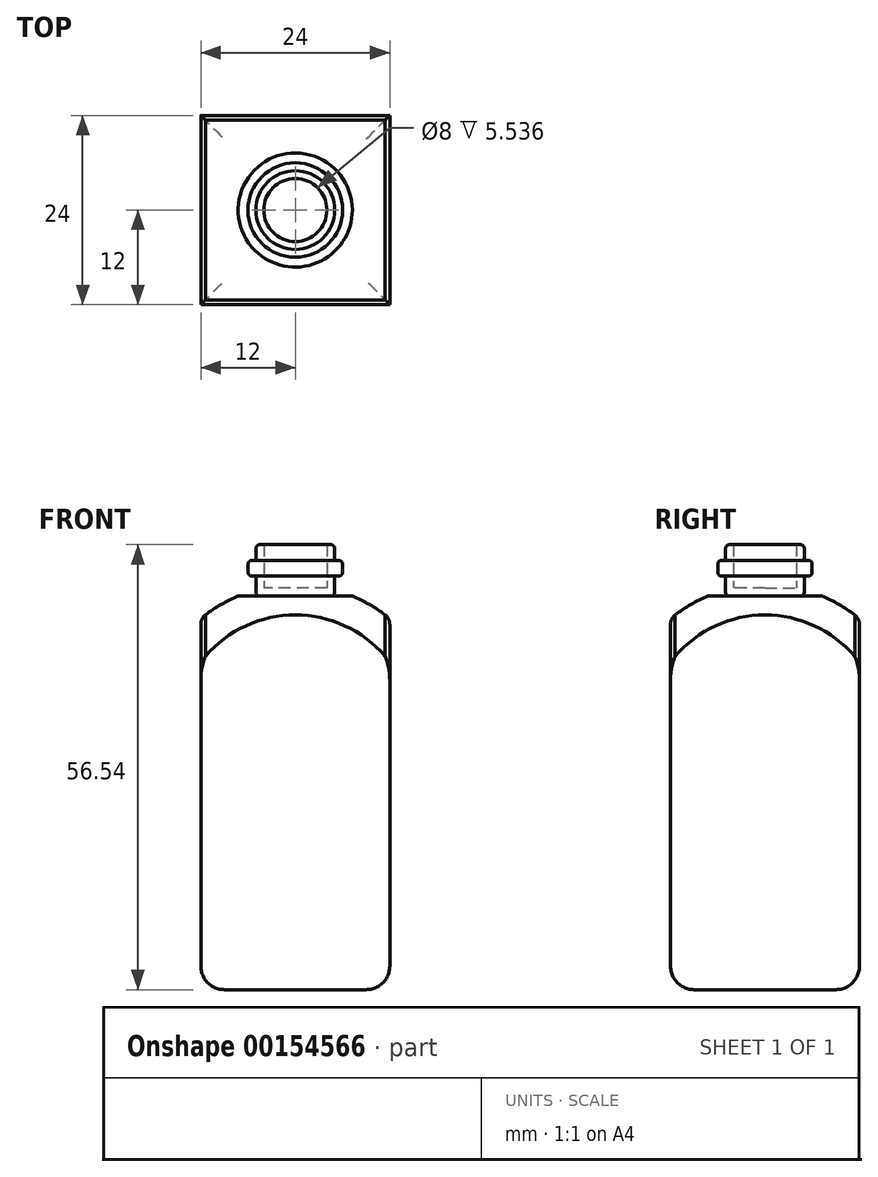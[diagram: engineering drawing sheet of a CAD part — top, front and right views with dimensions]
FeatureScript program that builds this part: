
annotation { "Feature Type Name" : "Feature", "Feature Type Description" : "" }
export const myFeature = defineFeature(function(context is Context, id is Id, definition is map)
    precondition{}
    {
        {
            var Q0;
            Q0=qCreatedBy(makeId("Front.planeOp"),FACE);
            var sketch = newSketch(context, id + "F0", { "sketchPlane" : qUnion([Q0])});
            skLineSegment(sketch, "E0", {"start": v(0, 56.54) * mm, "end": v(-5, 56.54) * mm});
            skLineSegment(sketch, "E1", {"start": v(-5, 56.54) * mm, "end": v(-5, 54.54) * mm});
            skLineSegment(sketch, "E2", {"start": v(-5, 54.54) * mm, "end": v(-6, 54.54) * mm});
            skLineSegment(sketch, "E3", {"start": v(-6, 54.54) * mm, "end": v(-6, 52.54) * mm});
            skLineSegment(sketch, "E4", {"start": v(-6, 52.54) * mm, "end": v(-5, 52.54) * mm});
            skLineSegment(sketch, "E5", {"start": v(-5, 52.54) * mm, "end": v(-5, 50) * mm});
            skLineSegment(sketch, "E6", {"start": v(-5, 50) * mm, "end": v(-12, 50) * mm});
            skLineSegment(sketch, "E7", {"start": v(-12, 50) * mm, "end": v(-12, 0) * mm});
            skLineSegment(sketch, "E8", {"start": v(-12, 0) * mm, "end": v(0, 0) * mm});
            skLineSegment(sketch, "E9", {"start": v(0, 0) * mm, "end": v(0, 56.54) * mm});
            skLineSegment(sketch, "E10.MirrorCS", {"start": v(5, 50) * mm, "end": v(12, 50) * mm});
            skLineSegment(sketch, "E11.MirrorCS", {"start": v(12, 50) * mm, "end": v(12, 0) * mm});
            skLineSegment(sketch, "E12.MirrorCS", {"start": v(12, 0) * mm, "end": v(0, 0) * mm});
            skLineSegment(sketch, "E13.MirrorCS", {"start": v(0, 56.54) * mm, "end": v(5, 56.54) * mm});
            skLineSegment(sketch, "E14.MirrorCS", {"start": v(5, 56.54) * mm, "end": v(5, 54.54) * mm});
            skLineSegment(sketch, "E15.MirrorCS", {"start": v(5, 54.54) * mm, "end": v(6, 54.54) * mm});
            skLineSegment(sketch, "E16.MirrorCS", {"start": v(6, 54.54) * mm, "end": v(6, 52.54) * mm});
            skLineSegment(sketch, "E17.MirrorCS", {"start": v(6, 52.54) * mm, "end": v(5, 52.54) * mm});
            skLineSegment(sketch, "E18.MirrorCS", {"start": v(5, 52.54) * mm, "end": v(5, 50) * mm});
            skLineSegment(sketch, "E19", {"start": v(-5, 50) * mm, "end": v(5, 50) * mm});
            skArc(sketch, "E20", {"start": v(-5, 50) * mm, "mid": v(-9.2, 47.2) * mm, "end": v(-12, 43) * mm});
            skPoint(sketch, "E21", {"position": v(0, 50) * mm});
            skSolve(sketch);
        }
        {
            var Q0;
            Q0=makeQuery(id+"F0.imprint","IMPRINT",FACE,{"disambiguationData":[TD([[makeQuery(id+"F0.imprint","IMPRINT",EDGE,{"derivedFrom":sQuery(id+"F0.wireOp",EDGE,"E9")}),-1.0]])]});
            var Q1;
            {var subQ4=sQuery(id+"F0.wireOp",EDGE,"E6");Q1=makeQuery(id+"F0.imprint","IMPRINT",FACE,{"disambiguationData":[TD([[makeQuery(id+"F0.imprint","IMPRINT",EDGE,{"derivedFrom":subQ4}),1.0]])]});}
            var Q2;
            {var subQ1=sQuery(id+"F0.wireOp",EDGE,"E8");Q2=makeQuery(id+"F0.imprint","IMPRINT",FACE,{"disambiguationData":[TD([[makeQuery(id+"F0.imprint","IMPRINT",EDGE,{"derivedFrom":subQ1}),1.0]])]});}
            extrude(context, id + "F1", {"entities" : qUnion([Q0, Q1, Q2]), "depth" : 12 * mm, "hasSecondDirection" : true, "secondDirectionOppositeDirection" : true, "secondDirectionDepth" : 12 * mm});
        }
        {
            var Q0;
            {var subQ1=sQuery(id+"F0.wireOp",EDGE,"E0");Q0=makeQuery(id+"F0.imprint","IMPRINT",FACE,{"disambiguationData":[TD([[makeQuery(id+"F0.imprint","IMPRINT",EDGE,{"derivedFrom":subQ1}),1.0]])]});}
            var Q1;
            Q1=sQuery(id+"F0.wireOp",EDGE,"E9");
            revolve(context, id + "F2", {"entities" : qUnion([Q0]), "axis" : qUnion([Q1]), "revolveType" : RevolveType.FULL});
        }
        {
            var Q0;
            Q0=makeQuery(id+"F2.opRevolve","SWEPT_EDGE",EDGE,{"disambiguationData":[OSD([sQuery(id+"F0.wireOp",EDGE,"E0"),sQuery(id+"F0.wireOp",EDGE,"E1")])]});
            var Q1;
            Q1=makeQuery(id+"F2.opRevolve","SWEPT_EDGE",EDGE,{"disambiguationData":[OSD([sQuery(id+"F0.wireOp",EDGE,"E2"),sQuery(id+"F0.wireOp",EDGE,"E3")])]});
            var Q2;
            Q2=makeQuery(id+"F2.opRevolve","SWEPT_EDGE",EDGE,{"disambiguationData":[OSD([sQuery(id+"F0.wireOp",EDGE,"E3"),sQuery(id+"F0.wireOp",EDGE,"E4")])]});
            var Q3;
            Q3=makeQuery(id+"F2.opRevolve","SWEPT_EDGE",EDGE,{"disambiguationData":[OSD([sQuery(id+"F0.wireOp",EDGE,"E5"),sQuery(id+"F0.wireOp",EDGE,"E6"),sQuery(id+"F0.wireOp",EDGE,"E19")])]});
            var Q4;
            Q4=makeQuery(id+"FP4xKetyCxuXSmg_1.boolean.opBoolean","COPY",EDGE,{"derivedFrom":makeQuery(id+"FP4xKetyCxuXSmg_1.boolean.toolComplement.opBoolean","COPY",EDGE,{"derivedFrom":makeQuery(id+"FP4xKetyCxuXSmg_1.opRevolve","SWEPT_EDGE",EDGE,{"disambiguationData":[OSD([sQuery(id+"F0.wireOp",EDGE,"E6"),sQuery(id+"F0.wireOp",EDGE,"SgCcnmhd-jZyr-n1Pt-VPxV-8aRdMBWvmJDz")])]})})});
            var Q5;
            Q5=makeQuery(id+"FP4xKetyCxuXSmg_1.boolean.opBoolean","COPY",EDGE,{"disambiguationData":[OD(0.0)],"derivedFrom":makeQuery(id+"FP4xKetyCxuXSmg_1.boolean.toolComplement.opBoolean","COPY",EDGE,{"derivedFrom":makeQuery(id+"FP4xKetyCxuXSmg_1.opRevolve","SWEPT_EDGE",EDGE,{"disambiguationData":[OSD([sQuery(id+"F0.wireOp",EDGE,"E7"),sQuery(id+"F0.wireOp",EDGE,"SgCcnmhd-jZyr-n1Pt-VPxV-8aRdMBWvmJDz")])]})})});
            var Q6;
            Q6=makeQuery(id+"FP4xKetyCxuXSmg_1.boolean.opBoolean","COPY",EDGE,{"disambiguationData":[OD(1.0)],"derivedFrom":makeQuery(id+"FP4xKetyCxuXSmg_1.boolean.toolComplement.opBoolean","COPY",EDGE,{"derivedFrom":makeQuery(id+"FP4xKetyCxuXSmg_1.opRevolve","SWEPT_EDGE",EDGE,{"disambiguationData":[OSD([sQuery(id+"F0.wireOp",EDGE,"E7"),sQuery(id+"F0.wireOp",EDGE,"SgCcnmhd-jZyr-n1Pt-VPxV-8aRdMBWvmJDz")])]})})});
            fillet(context, id + "F3", {"entities" : qUnion([Q0, Q1, Q2, Q3, Q4, Q5, Q6]), "radius" : .5 * mm, "allowEdgeOverflow" : false});
        }
        {
            var Q0;
            {var subQ0=sQuery(id+"F0.wireOp",EDGE,"E6");Q0=makeQuery(id+"F0.imprint","IMPRINT",FACE,{"disambiguationData":[TD([[makeQuery(id+"F0.imprint","IMPRINT",EDGE,{"derivedFrom":subQ0}),1.0]])]});}
            var Q1;
            Q1=sQuery(id+"F0.wireOp",EDGE,"E20");
            var Q2;
            Q2=sQuery(id+"F0.wireOp",EDGE,"E9");
            revolve(context, id + "F4", {"entities" : qUnion([Q0]), "surfaceEntities" : qUnion([Q1]), "axis" : qUnion([Q2]), "revolveType" : RevolveType.FULL, "oppositeDirection" : true});
        }
        {
            var Q0;
            Q0=makeQuery(id+"F4.opRevolve","SWEPT_BODY",BODY,{"disambiguationData":[OSD([sQuery(id+"F0.wireOp",EDGE,"E6"),sQuery(id+"F0.wireOp",EDGE,"E7"),sQuery(id+"F0.wireOp",EDGE,"E20")])]});
            var Q1;
            Q1=sQuery(id+"F0.wireOp",VERTEX,"E21");
            transform(context, id + "F5", {"entities" : qUnion([Q0]), "transformType" : TransformType.SCALE_UNIFORMLY, "scale" : 1.45, "scalePoint" : qUnion([Q1]), "makeCopy" : false});
        }
        {
            var Q0;
            Q0=makeQuery(id+"F4.opRevolve","SWEPT_BODY",BODY,{"disambiguationData":[OSD([sQuery(id+"F0.wireOp",EDGE,"E6"),sQuery(id+"F0.wireOp",EDGE,"E7"),sQuery(id+"F0.wireOp",EDGE,"E20")])]});
            var Q1;
            Q1=makeQuery(id+"F1.opExtrude","SWEPT_BODY",BODY,{"disambiguationData":[OSD([sQuery(id+"F0.wireOp",EDGE,"E6"),sQuery(id+"F0.wireOp",EDGE,"E7"),sQuery(id+"F0.wireOp",EDGE,"E8"),sQuery(id+"F0.wireOp",EDGE,"E10.MirrorCS"),sQuery(id+"F0.wireOp",EDGE,"E11.MirrorCS"),sQuery(id+"F0.wireOp",EDGE,"E12.MirrorCS"),sQuery(id+"F0.wireOp",EDGE,"E19")])]});
            booleanBodies(context, id + "F6", {"operationType" : BooleanOperationType.SUBTRACTION, "tools" : qUnion([Q0]), "targets" : qUnion([Q1])});
        }
        {
            var Q0;
            Q0=makeQuery(id+"F6.opBoolean","INTERSECT",EDGE,{"derivedFrom":[makeQuery(id+"F1.opExtrude","SWEPT_FACE",FACE,{"disambiguationData":[OSD([sQuery(id+"F0.wireOp",EDGE,"E11.MirrorCS")])]}),makeQuery(id+"F4.opRevolve","SWEPT_FACE",FACE,{"disambiguationData":[OSD([sQuery(id+"F0.wireOp",EDGE,"E20")])]})]});
            var Q1;
            Q1=makeQuery(id+"F6.opBoolean","INTERSECT",EDGE,{"derivedFrom":[makeQuery(id+"F1.opExtrude","CAP_FACE",FACE,{"disambiguationData":[OSD([sQuery(id+"F0.wireOp",EDGE,"E6"),sQuery(id+"F0.wireOp",EDGE,"E7"),sQuery(id+"F0.wireOp",EDGE,"E8"),sQuery(id+"F0.wireOp",EDGE,"E10.MirrorCS"),sQuery(id+"F0.wireOp",EDGE,"E11.MirrorCS"),sQuery(id+"F0.wireOp",EDGE,"E12.MirrorCS"),sQuery(id+"F0.wireOp",EDGE,"E19")])],"isStart":true}),makeQuery(id+"F4.opRevolve","SWEPT_FACE",FACE,{"disambiguationData":[OSD([sQuery(id+"F0.wireOp",EDGE,"E20")])]})]});
            var Q2;
            Q2=makeQuery(id+"F6.opBoolean","INTERSECT",EDGE,{"derivedFrom":[makeQuery(id+"F1.opExtrude","SWEPT_FACE",FACE,{"disambiguationData":[OSD([sQuery(id+"F0.wireOp",EDGE,"E7")])]}),makeQuery(id+"F4.opRevolve","SWEPT_FACE",FACE,{"disambiguationData":[OSD([sQuery(id+"F0.wireOp",EDGE,"E20")])]})]});
            var Q3;
            Q3=makeQuery(id+"F6.opBoolean","INTERSECT",EDGE,{"derivedFrom":[makeQuery(id+"F1.opExtrude","CAP_FACE",FACE,{"disambiguationData":[OSD([sQuery(id+"F0.wireOp",EDGE,"E6"),sQuery(id+"F0.wireOp",EDGE,"E7"),sQuery(id+"F0.wireOp",EDGE,"E8"),sQuery(id+"F0.wireOp",EDGE,"E10.MirrorCS"),sQuery(id+"F0.wireOp",EDGE,"E11.MirrorCS"),sQuery(id+"F0.wireOp",EDGE,"E12.MirrorCS"),sQuery(id+"F0.wireOp",EDGE,"E19")])],"isStart":false}),makeQuery(id+"F4.opRevolve","SWEPT_FACE",FACE,{"disambiguationData":[OSD([sQuery(id+"F0.wireOp",EDGE,"E20")])]})]});
            fillet(context, id + "F7", {"entities" : qUnion([Q0, Q1, Q2, Q3]), "radius" : 1.5 * mm, "tangentPropagation" : true, "allowEdgeOverflow" : false});
        }
        {
            var Q0;
            Q0=makeQuery(id+"F1.opExtrude","SWEPT_EDGE",EDGE,{"disambiguationData":[OSD([sQuery(id+"F0.wireOp",EDGE,"E7"),sQuery(id+"F0.wireOp",EDGE,"E8")])]});
            var Q1;
            Q1=makeQuery(id+"F1.opExtrude","CAP_EDGE",EDGE,{"disambiguationData":[OSD([sQuery(id+"F0.wireOp",EDGE,"E8"),sQuery(id+"F0.wireOp",EDGE,"E12.MirrorCS")])],"isStart":true});
            var Q2;
            Q2=makeQuery(id+"F1.opExtrude","SWEPT_EDGE",EDGE,{"disambiguationData":[OSD([sQuery(id+"F0.wireOp",EDGE,"E11.MirrorCS"),sQuery(id+"F0.wireOp",EDGE,"E12.MirrorCS")])]});
            var Q3;
            Q3=makeQuery(id+"F1.opExtrude","CAP_EDGE",EDGE,{"disambiguationData":[OSD([sQuery(id+"F0.wireOp",EDGE,"E8"),sQuery(id+"F0.wireOp",EDGE,"E12.MirrorCS")])],"isStart":false});
            fillet(context, id + "F8", {"entities" : qUnion([Q0, Q1, Q2, Q3]), "radius" : 3 * mm, "tangentPropagation" : true, "allowEdgeOverflow" : false});
        }
        {
            var Q0;
            Q0=makeQuery(id+"F2.opRevolve","SWEPT_FACE",FACE,{"disambiguationData":[OSD([sQuery(id+"F0.wireOp",EDGE,"E0")])]});
            shell(context, id + "F9", {"entities" : qUnion([Q0]), "thickness" : 1 * mm});
        }
    });
